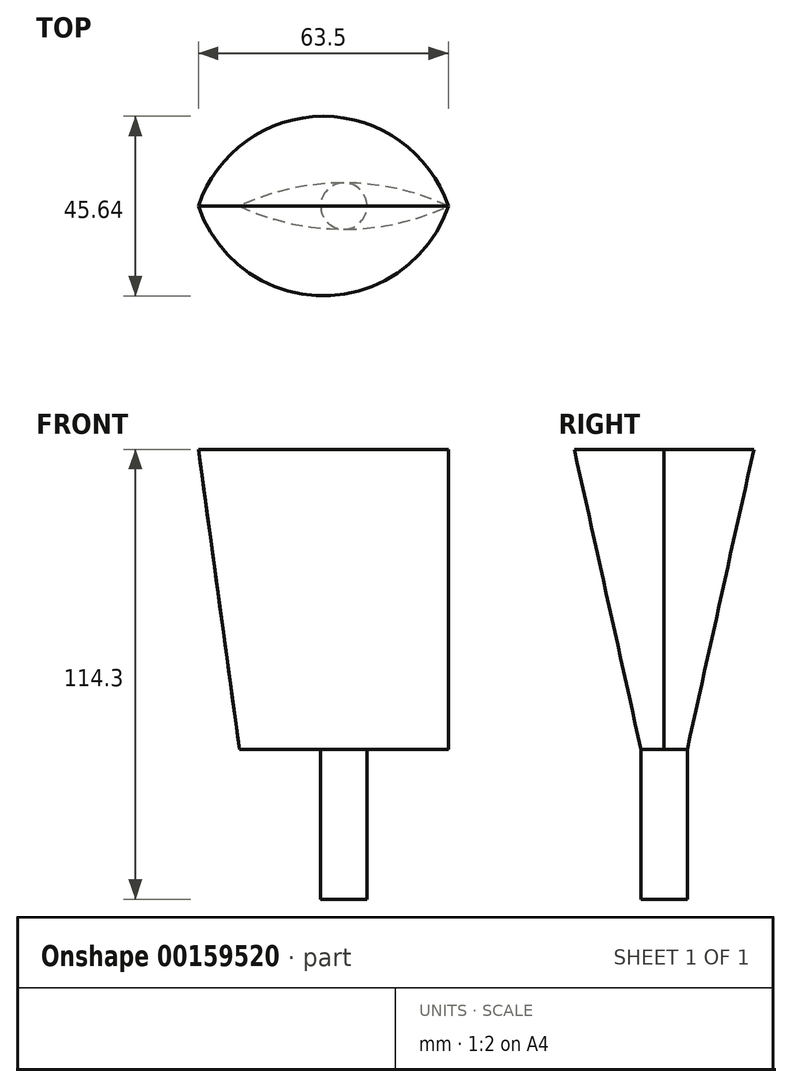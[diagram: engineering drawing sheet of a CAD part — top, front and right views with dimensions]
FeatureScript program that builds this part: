
annotation { "Feature Type Name" : "Feature", "Feature Type Description" : "" }
export const myFeature = defineFeature(function(context is Context, id is Id, definition is map)
    precondition{}
    {
        {
            var Q0;
            Q0=qCreatedBy(makeId("Top.planeOp"),FACE);
            var sketch = newSketch(context, id + "F0", { "sketchPlane" : qUnion([Q0])});
            skLineSegment(sketch, "E0.bottom", {"start": v(0, 0) * mm, "end": v(-53.06, 0) * mm});
            skArc(sketch, "E1", {"start": v(0, 0) * mm, "mid": v(-26.53, 5.88) * mm, "end": v(-53.06, 0) * mm});
            skSolve(sketch);
        }
        {
            var Q0;
            Q0=qCreatedBy(makeId("Top.planeOp"),FACE);
            cPlane(context, id + "F1", {"entities" : qUnion([Q0]), "cplaneType" : CPlaneType.OFFSET, "offset" : 76.2 * mm, "width" : 152.4 * mm, "height" : 152.4 * mm});
        }
        {
            var Q0;
            Q0=qCreatedBy(id+"F1.planeOp",FACE);
            var sketch = newSketch(context, id + "F2", { "sketchPlane" : qUnion([Q0])});
            skLineSegment(sketch, "E2", {"start": v(-63.5, 0) * mm, "end": v(0, 0) * mm});
            skArc(sketch, "E3", {"start": v(0, 0) * mm, "mid": v(-31.75, 22.82) * mm, "end": v(-63.5, 0) * mm});
            skSolve(sketch);
        }
        {
            var Q0;
            Q0=makeQuery(id+"F0.imprint","IMPRINT",FACE,{"disambiguationData":[TD([[makeQuery(id+"F0.imprint","IMPRINT",EDGE,{"derivedFrom":sQuery(id+"F0.wireOp",EDGE,"E0.bottom")}),-1.0]])]});
            var Q1;
            Q1=makeQuery(id+"F2.imprint","IMPRINT",FACE,{"disambiguationData":[TD([[makeQuery(id+"F2.imprint","IMPRINT",EDGE,{"derivedFrom":sQuery(id+"F2.wireOp",EDGE,"E2")}),1.0]])]});
            loft(context, id + "F3", {"sheetProfilesArray" : [{ "sheetProfileEntities" : qUnion([Q0]) }, { "sheetProfileEntities" : qUnion([Q1]) }]});
        }
        {
            var Q0;
            Q0=makeQuery(id+"F3.opLoft","SWEPT_BODY",BODY,{"disambiguationData":[OSD([makeQuery(id+"F0.imprint","IMPRINT",FACE,{"disambiguationData":[TD([[makeQuery(id+"F0.imprint","IMPRINT",EDGE,{"derivedFrom":sQuery(id+"F0.wireOp",EDGE,"E0.bottom")}),-1.0]])]}),makeQuery(id+"F2.imprint","IMPRINT",FACE,{"disambiguationData":[TD([[makeQuery(id+"F2.imprint","IMPRINT",EDGE,{"derivedFrom":sQuery(id+"F2.wireOp",EDGE,"E2")}),1.0]])]})])]});
            var Q1;
            Q1=qCreatedBy(makeId("Front.planeOp"),FACE);
            mirror(context, id + "F4", {"entities" : qUnion([Q0]), "mirrorPlane" : qUnion([Q1])});
        }
        {
            var Q0;
            Q0=makeQuery(id+"F3.opLoft","CAP_FACE",FACE,{"disambiguationData":[OSD([makeQuery(id+"F0.imprint","IMPRINT",FACE,{"disambiguationData":[TD([[makeQuery(id+"F0.imprint","IMPRINT",EDGE,{"derivedFrom":sQuery(id+"F0.wireOp",EDGE,"E0.bottom")}),-1.0]])]})])],"isStart":true});
            var sketch = newSketch(context, id + "F5", { "sketchPlane" : qUnion([Q0])});
            skCircle(sketch, "E4", {"center": v(-26.53, 0) * mm, "radius": 5.88 * mm});
            skSolve(sketch);
        }
        {
            var Q0;
            {var subQ0=sQuery(id+"F5.wireOp",EDGE,"E4");var subQ1=sQuery(id+"F0.wireOp",EDGE,"E0.bottom");var subQ2=sQuery(id+"F0.wireOp",EDGE,"E1");var subQ3=makeQuery(id+"F3.opLoft","MID_CAP_EDGE",EDGE,{"disambiguationData":[OSD([subQ1,subQ2]),TDD([makeQuery(id+"F0.imprint","INTERSECT",VERTEX,{"disambiguationData":[OD(0.0)],"derivedFrom":[subQ1,subQ2]}),makeQuery(id+"F0.imprint","INTERSECT",VERTEX,{"disambiguationData":[OD(1.0)],"derivedFrom":[subQ1,subQ2]}),makeQuery(id+"F0.imprint","IMPRINT",EDGE,{"derivedFrom":subQ1})])],"capPos":0.0});var subQ4=makeQuery(id+"F5.imprint","INTERSECT",VERTEX,{"disambiguationData":[OD(0.0)],"derivedFrom":[subQ3,subQ0]});Q0=makeQuery(id+"F5.imprint","IMPRINT",FACE,{"disambiguationData":[TD([[makeQuery(id+"F5.imprint","IMPRINT",EDGE,{"disambiguationData":[TD([[subQ4,1.0]])],"derivedFrom":subQ0}),1.0]])]});}
            var Q1;
            {var subQ0=sQuery(id+"F5.wireOp",EDGE,"E4");var subQ1=sQuery(id+"F0.wireOp",EDGE,"E0.bottom");var subQ2=sQuery(id+"F0.wireOp",EDGE,"E1");var subQ3=makeQuery(id+"F0.imprint","INTERSECT",VERTEX,{"disambiguationData":[OD(1.0)],"derivedFrom":[subQ1,subQ2]});var subQ4=makeQuery(id+"F0.imprint","INTERSECT",VERTEX,{"disambiguationData":[OD(0.0)],"derivedFrom":[subQ1,subQ2]});var subQ5=makeQuery(id+"F3.opLoft","MID_CAP_EDGE",EDGE,{"disambiguationData":[OSD([subQ1,subQ2]),TDD([subQ4,subQ3,makeQuery(id+"F0.imprint","IMPRINT",EDGE,{"derivedFrom":subQ1})])],"capPos":0.0});var subQ6=makeQuery(id+"F5.imprint","INTERSECT",VERTEX,{"disambiguationData":[OD(0.0)],"derivedFrom":[subQ5,subQ0]});Q1=makeQuery(id+"F5.imprint","IMPRINT",FACE,{"disambiguationData":[TD([[makeQuery(id+"F5.imprint","IMPRINT",EDGE,{"disambiguationData":[TD([[subQ6,-1.0]])],"derivedFrom":subQ0}),1.0]])]});}
            extrude(context, id + "F6", {"entities" : qUnion([Q0, Q1]), "depth" : 38.1 * mm});
        }
        {
            var Q0;
            Q0=qCreatedBy(makeId("Front.planeOp"),FACE);
            var sketch = newSketch(context, id + "F7", { "sketchPlane" : qUnion([Q0])});
            skLineSegment(sketch, "E5.bottom", {"start": v(14.44, 0) * mm, "end": v(60.68, 0) * mm});
            skLineSegment(sketch, "E5.top", {"start": v(14.44, 23.66) * mm, "end": v(60.68, 23.66) * mm});
            skLineSegment(sketch, "E5.left", {"start": v(14.44, 0) * mm, "end": v(14.44, 23.66) * mm});
            skLineSegment(sketch, "E5.right", {"start": v(60.68, 0) * mm, "end": v(60.68, 23.66) * mm});
            skSolve(sketch);
        }
        {
            var Q0;
            Q0=makeQuery(id+"F7.imprint","IMPRINT",FACE,{"disambiguationData":[TD([[makeQuery(id+"F7.imprint","IMPRINT",EDGE,{"derivedFrom":sQuery(id+"F7.wireOp",EDGE,"E5.bottom")}),1.0]])]});
            extrude(context, id + "F8", {"entities" : qUnion([Q0]), "depth" : 26.03 * mm});
        }
        {
            var Q0;
            Q0=makeQuery(id+"F8.opExtrude","SWEPT_BODY",BODY,{"disambiguationData":[OSD([sQuery(id+"F7.wireOp",EDGE,"E5.bottom"),sQuery(id+"F7.wireOp",EDGE,"E5.top"),sQuery(id+"F7.wireOp",EDGE,"E5.left"),sQuery(id+"F7.wireOp",EDGE,"E5.right")])]});
            deleteBodies(context, id + "F9", {"entities" : qUnion([Q0])});
        }
    });
